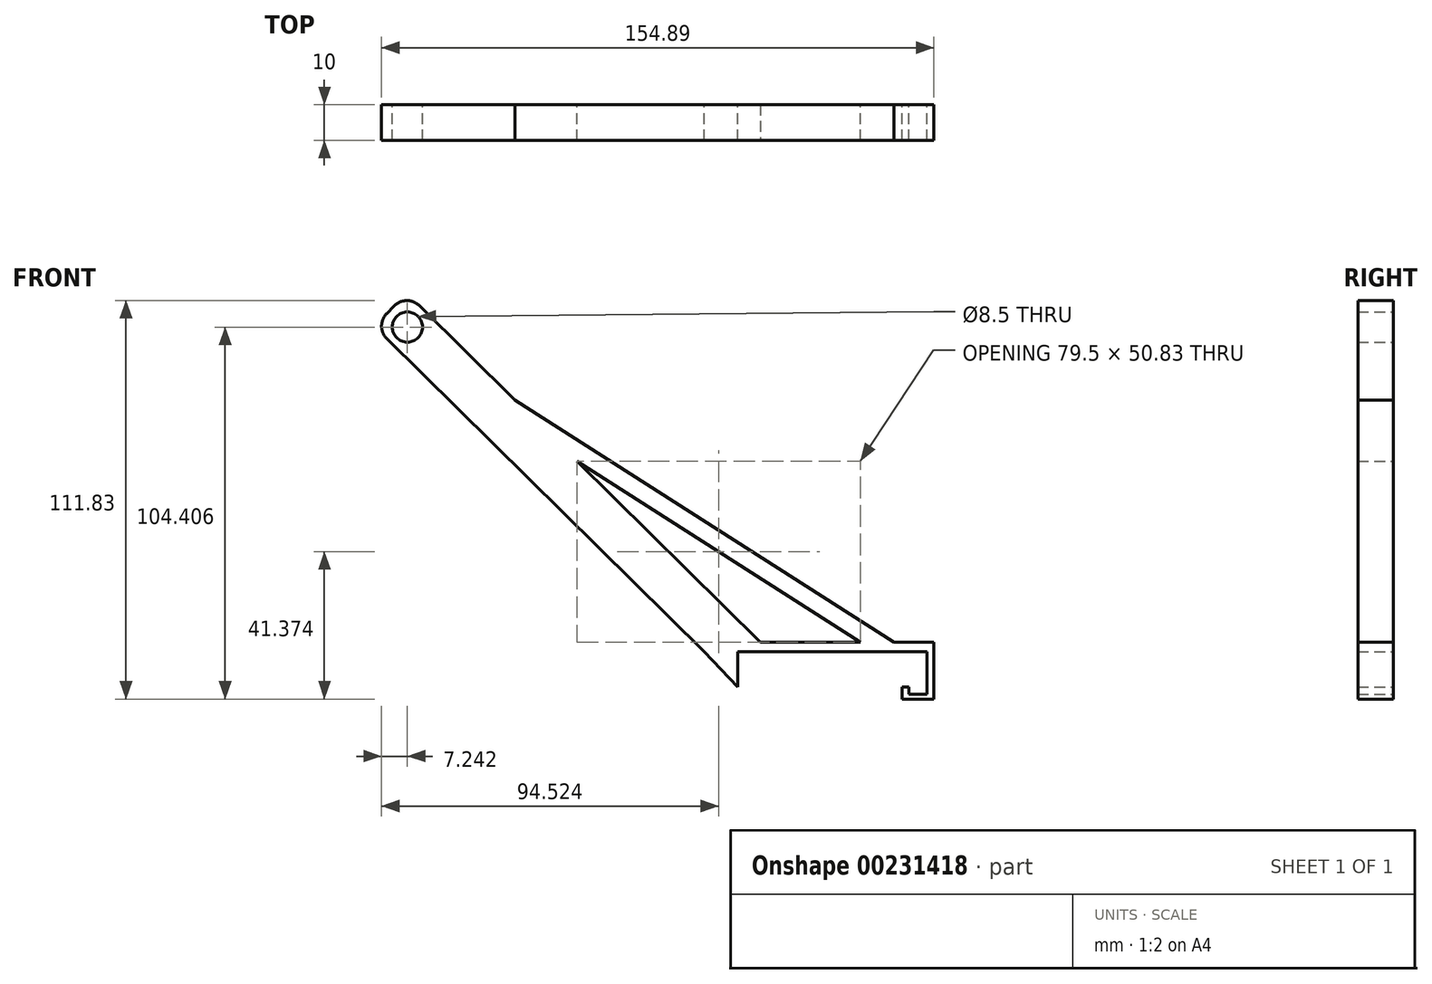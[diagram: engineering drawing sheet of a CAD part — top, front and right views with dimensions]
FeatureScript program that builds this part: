
annotation { "Feature Type Name" : "Feature", "Feature Type Description" : "" }
export const myFeature = defineFeature(function(context is Context, id is Id, definition is map)
    precondition{}
    {
        {
            var Q0;
            Q0=qCreatedBy(makeId("Front.planeOp"),FACE);
            var sketch = newSketch(context, id + "F0", { "sketchPlane" : qUnion([Q0])});
            skLineSegment(sketch, "E0", {"start": v(-1.28, -35.78) * mm, "end": v(7.67, -35.78) * mm});
            skLineSegment(sketch, "E1", {"start": v(7.67, -35.78) * mm, "end": v(7.67, -19.82) * mm});
            skLineSegment(sketch, "E2", {"start": v(7.67, -19.82) * mm, "end": v(-47.28, -19.82) * mm});
            skLineSegment(sketch, "E3", {"start": v(-47.28, -19.82) * mm, "end": v(-47.28, -22.46) * mm});
            skLineSegment(sketch, "E4", {"start": v(-47.28, -22.46) * mm, "end": v(5.72, -22.46) * mm});
            skLineSegment(sketch, "E5", {"start": v(5.72, -22.46) * mm, "end": v(5.72, -34.46) * mm});
            skLineSegment(sketch, "E6", {"start": v(5.72, -34.46) * mm, "end": v(0.72, -34.46) * mm});
            skLineSegment(sketch, "E7", {"start": v(0.72, -34.46) * mm, "end": v(0.72, -32.46) * mm});
            skLineSegment(sketch, "E8", {"start": v(0.72, -32.46) * mm, "end": v(-1.28, -32.46) * mm});
            skLineSegment(sketch, "E9", {"start": v(-1.28, -32.46) * mm, "end": v(-1.28, -35.78) * mm});
            skLineSegment(sketch, "E10", {"start": v(-47.28, -22.46) * mm, "end": v(-47.28, -32.46) * mm});
            skLineSegment(sketch, "E11", {"start": v(-47.28, -32.46) * mm, "end": v(-56.78, -22.46) * mm});
            skLineSegment(sketch, "E12", {"start": v(-56.78, -22.46) * mm, "end": v(-47.28, -22.46) * mm});
            skLineSegment(sketch, "E13", {"start": v(-56.78, -19.82) * mm, "end": v(-56.78, -22.46) * mm});
            skLineSegment(sketch, "E14", {"start": v(-47.28, -19.82) * mm, "end": v(-56.78, -19.82) * mm});
            skSolve(sketch);
        }
        {
            var Q0;
            Q0=qCreatedBy(makeId("Front.planeOp"),FACE);
            var sketch = newSketch(context, id + "F1", { "sketchPlane" : qUnion([Q0])});
            skLineSegment(sketch, "E15", {"start": v(-56.78, -22.46) * mm, "end": v(-145.73, 65.36) * mm});
            skLineSegment(sketch, "E16", {"start": v(-145.78, 72.43) * mm, "end": v(-143.67, 74.56) * mm});
            skLineSegment(sketch, "E17", {"start": v(-136.6, 74.6) * mm, "end": v(-40.58, -20.2) * mm});
            skLineSegment(sketch, "E18", {"start": v(-40.58, -20.2) * mm, "end": v(-56.78, -22.46) * mm});
            skPoint(sketch, "E19.visualSharp", {"position": v(-140.16, 78.12) * mm});
            skArc(sketch, "E19.filletArc", {"start": v(-136.6, 74.6) * mm, "mid": v(-140.15, 76.05) * mm, "end": v(-143.67, 74.56) * mm});
            skPoint(sketch, "E20.visualSharp", {"position": v(-149.29, 68.87) * mm});
            skArc(sketch, "E20.filletArc", {"start": v(-145.78, 72.43) * mm, "mid": v(-147.22, 68.88) * mm, "end": v(-145.73, 65.36) * mm});
            skCircle(sketch, "E21", {"center": v(-139.98, 68.63) * mm, "radius": 4.25 * mm});
            skSolve(sketch);
        }
        {
            var Q0;
            Q0 = qSketchRegion(id + "F0", true);
            var Q1;
            Q1 = qSketchRegion(id + "F1", true);
            extrude(context, id + "F2", {"entities" : qUnion([Q0, Q1]), "depth" : 10 * mm});
        }
        {
            var Q0;
            Q0=qCreatedBy(makeId("Front.planeOp"),FACE);
            var sketch = newSketch(context, id + "F3", { "sketchPlane" : qUnion([Q0])});
            skLineSegment(sketch, "E22", {"start": v(-118.45, 53.67) * mm, "end": v(-2.5, -20.46) * mm});
            skLineSegment(sketch, "E23", {"start": v(-2.5, -20.46) * mm, "end": v(-11.95, -20.46) * mm});
            skLineSegment(sketch, "E24", {"start": v(-11.95, -20.46) * mm, "end": v(-116.22, 46.21) * mm});
            skLineSegment(sketch, "E25", {"start": v(-116.22, 46.21) * mm, "end": v(-118.45, 53.67) * mm});
            skSolve(sketch);
        }
        {
            var Q0;
            Q0 = qSketchRegion(id + "F3", true);
            extrude(context, id + "F4", {"entities" : qUnion([Q0]), "operationType" : NewBodyOperationType.ADD, "depth" : 10 * mm});
        }
    });
